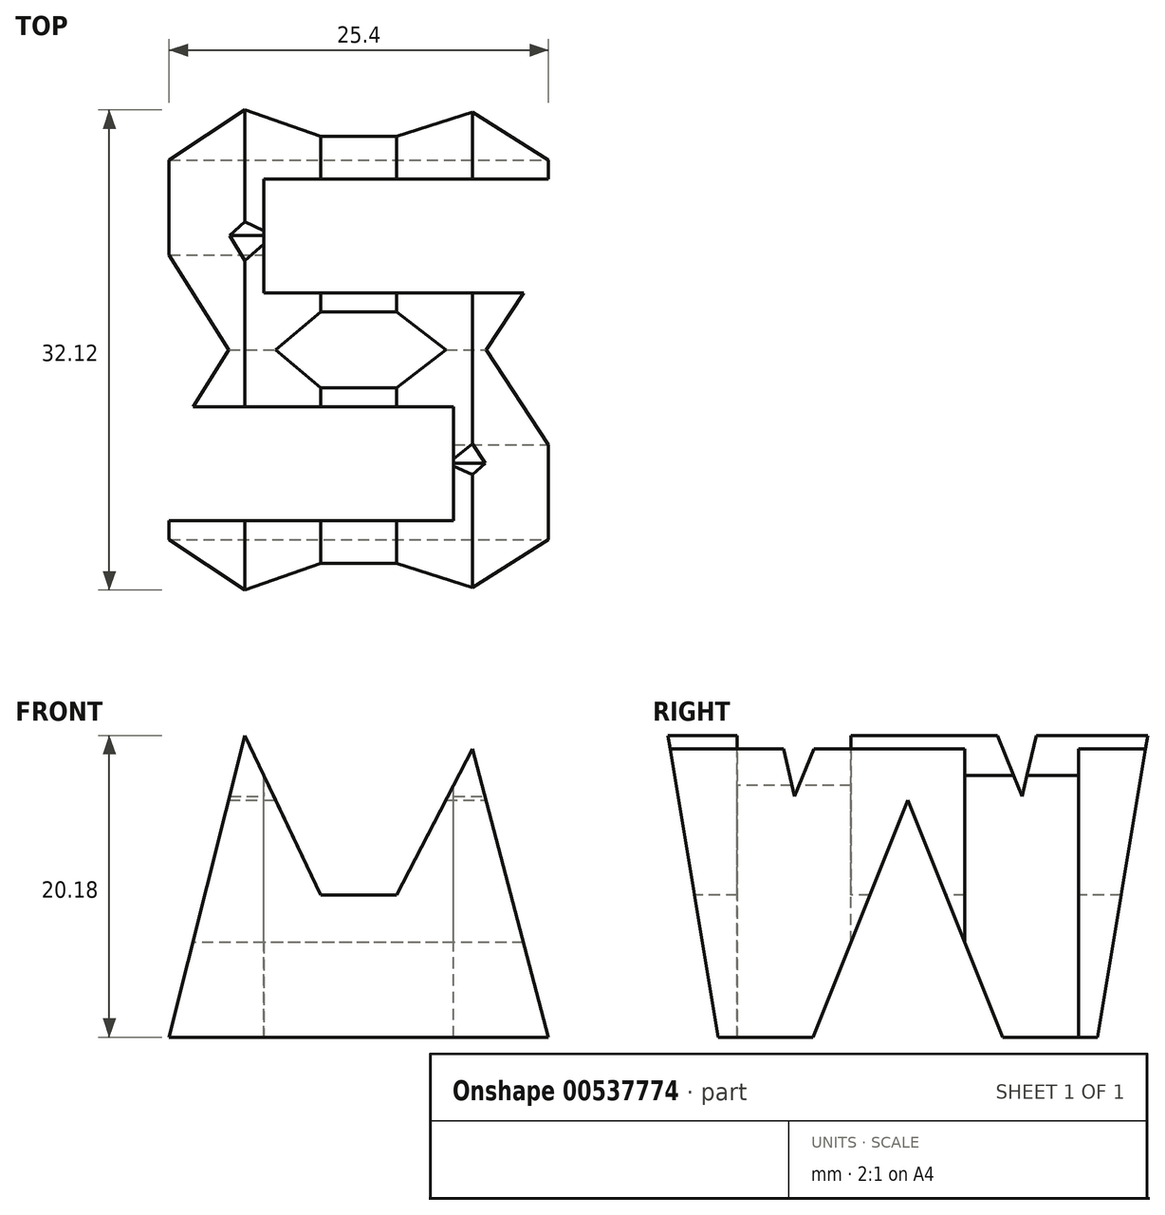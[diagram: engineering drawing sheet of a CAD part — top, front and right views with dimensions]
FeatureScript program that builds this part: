
annotation { "Feature Type Name" : "Feature", "Feature Type Description" : "" }
export const myFeature = defineFeature(function(context is Context, id is Id, definition is map)
    precondition{}
    {
        {
            var Q0;
            Q0=qCreatedBy(makeId("Front.planeOp"),FACE);
            var sketch = newSketch(context, id + "F0", { "sketchPlane" : qUnion([Q0])});
            skLineSegment(sketch, "E0", {"start": v(0, 0) * mm, "end": v(0, 38.1) * mm});
            skLineSegment(sketch, "E1", {"start": v(38.1, 38.1) * mm, "end": v(38.1, 0) * mm});
            skLineSegment(sketch, "E2", {"start": v(0, 0) * mm, "end": v(38.1, 0) * mm});
            skLineSegment(sketch, "E3", {"start": v(0, 38.1) * mm, "end": v(38.1, 38.1) * mm});
            skSolve(sketch);
        }
        {
            var Q0;
            Q0 = qSketchRegion(id + "F0", true);
            extrude(context, id + "F1", {"entities" : qUnion([Q0]), "depth" : 38.1 * mm, "offsetDistance" : 25.4 * mm});
        }
        {
            var Q0;
            Q0=qCreatedBy(makeId("Front.planeOp"),FACE);
            cPlane(context, id + "F2", {"entities" : qUnion([Q0]), "cplaneType" : CPlaneType.OFFSET, "offset" : 38.1 * mm, "width" : 152.4 * mm, "height" : 152.4 * mm});
        }
        {
            var Q0;
            Q0=qCreatedBy(makeId("Right.planeOp"),FACE);
            cPlane(context, id + "F3", {"entities" : qUnion([Q0]), "cplaneType" : CPlaneType.OFFSET, "offset" : 38.1 * mm, "width" : 152.4 * mm, "height" : 152.4 * mm});
        }
        {
            var Q0;
            Q0=qCreatedBy(makeId("Top.planeOp"),FACE);
            cPlane(context, id + "F4", {"entities" : qUnion([Q0]), "cplaneType" : CPlaneType.OFFSET, "offset" : 38.1 * mm, "width" : 152.4 * mm, "height" : 152.4 * mm});
        }
        {
            var Q0;
            Q0=qCreatedBy(id+"F3.planeOp",FACE);
            var sketch = newSketch(context, id + "F5", { "sketchPlane" : qUnion([Q0])});
            skLineSegment(sketch, "E4.bottom", {"start": v(0, 0) * mm, "end": v(-38.1, 0) * mm});
            skLineSegment(sketch, "E4.top", {"start": v(0, 38.1) * mm, "end": v(-38.1, 38.1) * mm});
            skLineSegment(sketch, "E4.left", {"start": v(0, 0) * mm, "end": v(0, 38.1) * mm});
            skLineSegment(sketch, "E4.right", {"start": v(-38.1, 0) * mm, "end": v(-38.1, 38.1) * mm});
            skLineSegment(sketch, "E5", {"start": v(-38.1, 38.1) * mm, "end": v(-31.75, 0) * mm});
            skLineSegment(sketch, "E6", {"start": v(-31.75, 38.1) * mm, "end": v(-26.64, 16.1) * mm});
            skLineSegment(sketch, "E7", {"start": v(-26.64, 16.1) * mm, "end": v(-21.56, 28.58) * mm});
            skLineSegment(sketch, "E8", {"start": v(-21.56, 28.58) * mm, "end": v(-16.48, 28.58) * mm});
            skLineSegment(sketch, "E9", {"start": v(-16.48, 28.58) * mm, "end": v(-11.4, 16.1) * mm});
            skLineSegment(sketch, "E10", {"start": v(-11.4, 16.1) * mm, "end": v(-6.35, 38.1) * mm});
            skLineSegment(sketch, "E11", {"start": v(0, 38.1) * mm, "end": v(-6.35, 0) * mm});
            skLineSegment(sketch, "E12", {"start": v(-31.75, 0) * mm, "end": v(-25.4, 0) * mm});
            skLineSegment(sketch, "E13", {"start": v(-25.4, 0) * mm, "end": v(-19.05, 15.88) * mm});
            skLineSegment(sketch, "E14", {"start": v(-19.05, 15.88) * mm, "end": v(-12.7, 0) * mm});
            skLineSegment(sketch, "E15", {"start": v(-12.7, 0) * mm, "end": v(-6.35, 0) * mm});
            skSolve(sketch);
        }
        {
            var Q0;
            {var subQ0=sQuery(id+"F5.wireOp",EDGE,"E6");Q0=makeQuery(id+"F5.imprint","IMPRINT",FACE,{"disambiguationData":[TD([[makeQuery(id+"F5.imprint","IMPRINT",EDGE,{"derivedFrom":subQ0}),1.0]])]});}
            var Q1;
            {var subQ0=sQuery(id+"F5.wireOp",EDGE,"E4.left");Q1=makeQuery(id+"F5.imprint","IMPRINT",FACE,{"disambiguationData":[TD([[makeQuery(id+"F5.imprint","IMPRINT",EDGE,{"derivedFrom":subQ0}),1.0]])]});}
            var Q2;
            {var subQ0=sQuery(id+"F5.wireOp",EDGE,"E13");Q2=makeQuery(id+"F5.imprint","IMPRINT",FACE,{"disambiguationData":[TD([[makeQuery(id+"F5.imprint","IMPRINT",EDGE,{"derivedFrom":subQ0}),-1.0]])]});}
            var Q3;
            {var subQ0=sQuery(id+"F5.wireOp",EDGE,"E4.right");Q3=makeQuery(id+"F5.imprint","IMPRINT",FACE,{"disambiguationData":[TD([[makeQuery(id+"F5.imprint","IMPRINT",EDGE,{"derivedFrom":subQ0}),-1.0]])]});}
            extrude(context, id + "F6", {"entities" : qUnion([Q0, Q1, Q2, Q3]), "operationType" : NewBodyOperationType.REMOVE, "oppositeDirection" : true, "depth" : 38.1 * mm, "offsetDistance" : 25.4 * mm});
        }
        {
            var Q0;
            Q0=qCreatedBy(id+"F2.planeOp",FACE);
            var sketch = newSketch(context, id + "F7", { "sketchPlane" : qUnion([Q0])});
            skLineSegment(sketch, "E16", {"start": v(0, 0) * mm, "end": v(0, 38.1) * mm});
            skLineSegment(sketch, "E17", {"start": v(0, 38.1) * mm, "end": v(38.1, 38.1) * mm});
            skLineSegment(sketch, "E18", {"start": v(38.1, 38.1) * mm, "end": v(38.1, 0) * mm});
            skLineSegment(sketch, "E19", {"start": v(38.1, 0) * mm, "end": v(0, 0) * mm});
            skLineSegment(sketch, "E20", {"start": v(38.1, 0) * mm, "end": v(31.75, 38.1) * mm});
            skLineSegment(sketch, "E21", {"start": v(31.75, 38.1) * mm, "end": v(25.4, 38.1) * mm});
            skLineSegment(sketch, "E22", {"start": v(25.4, 38.1) * mm, "end": v(19.05, 22.22) * mm});
            skLineSegment(sketch, "E23", {"start": v(19.05, 22.22) * mm, "end": v(12.7, 38.1) * mm});
            skLineSegment(sketch, "E24", {"start": v(12.7, 38.1) * mm, "end": v(6.35, 38.1) * mm});
            skLineSegment(sketch, "E25", {"start": v(6.35, 38.1) * mm, "end": v(0, 0) * mm});
            skLineSegment(sketch, "E26", {"start": v(38.1, 0) * mm, "end": v(31.75, 0) * mm});
            skLineSegment(sketch, "E27", {"start": v(6.35, 0) * mm, "end": v(0, 0) * mm});
            skLineSegment(sketch, "E28", {"start": v(31.75, 0) * mm, "end": v(26.67, 19.3) * mm});
            skLineSegment(sketch, "E29", {"start": v(26.67, 19.3) * mm, "end": v(21.6, 9.52) * mm});
            skLineSegment(sketch, "E30", {"start": v(21.6, 9.52) * mm, "end": v(16.51, 9.52) * mm});
            skLineSegment(sketch, "E31", {"start": v(16.51, 9.52) * mm, "end": v(11.43, 20.18) * mm});
            skLineSegment(sketch, "E32", {"start": v(11.43, 20.18) * mm, "end": v(6.35, 0) * mm});
            skSolve(sketch);
        }
        {
            var Q0;
            {var subQ0=sQuery(id+"F7.wireOp",EDGE,"E16");Q0=makeQuery(id+"F7.imprint","IMPRINT",FACE,{"disambiguationData":[TD([[makeQuery(id+"F7.imprint","IMPRINT",EDGE,{"derivedFrom":subQ0}),-1.0]])]});}
            var Q1;
            {var subQ0=sQuery(id+"F7.wireOp",EDGE,"E22");Q1=makeQuery(id+"F7.imprint","IMPRINT",FACE,{"disambiguationData":[TD([[makeQuery(id+"F7.imprint","IMPRINT",EDGE,{"derivedFrom":subQ0}),-1.0]])]});}
            var Q2;
            {var subQ0=sQuery(id+"F7.wireOp",EDGE,"E18");Q2=makeQuery(id+"F7.imprint","IMPRINT",FACE,{"disambiguationData":[TD([[makeQuery(id+"F7.imprint","IMPRINT",EDGE,{"derivedFrom":subQ0}),-1.0]])]});}
            var Q3;
            Q3=makeQuery(id+"F7.imprint","IMPRINT",FACE,{"disambiguationData":[TD([[makeQuery(id+"F7.imprint","IMPRINT",EDGE,{"derivedFrom":sQuery(id+"F7.wireOp",EDGE,"E19")}),-1.0]])]});
            extrude(context, id + "F8", {"entities" : qUnion([Q0, Q1, Q2, Q3]), "operationType" : NewBodyOperationType.REMOVE, "oppositeDirection" : true, "depth" : 38.1 * mm, "offsetDistance" : 25.4 * mm});
        }
        {
            var Q0;
            Q0=qCreatedBy(id+"F4.planeOp",FACE);
            var sketch = newSketch(context, id + "F9", { "sketchPlane" : qUnion([Q0])});
            skLineSegment(sketch, "E33", {"start": v(0, 0) * mm, "end": v(0, -38.1) * mm});
            skLineSegment(sketch, "E34", {"start": v(0, -38.1) * mm, "end": v(38.1, -38.1) * mm});
            skLineSegment(sketch, "E35", {"start": v(38.1, -38.1) * mm, "end": v(38.1, 0) * mm});
            skLineSegment(sketch, "E36", {"start": v(38.1, 0) * mm, "end": v(0, 0) * mm});
            skLineSegment(sketch, "E37", {"start": v(38.1, -7.62) * mm, "end": v(12.7, -7.62) * mm});
            skLineSegment(sketch, "E38", {"start": v(12.7, -7.62) * mm, "end": v(12.7, -15.24) * mm});
            skLineSegment(sketch, "E39", {"start": v(12.7, -15.24) * mm, "end": v(38.1, -15.24) * mm});
            skLineSegment(sketch, "E40", {"start": v(0, -22.86) * mm, "end": v(25.4, -22.86) * mm});
            skLineSegment(sketch, "E41", {"start": v(25.4, -22.86) * mm, "end": v(25.4, -30.48) * mm});
            skLineSegment(sketch, "E42", {"start": v(25.4, -30.48) * mm, "end": v(0, -30.48) * mm});
            skSolve(sketch);
        }
        {
            var Q0;
            {var subQ0=sQuery(id+"F9.wireOp",EDGE,"E40");Q0=makeQuery(id+"F9.imprint","IMPRINT",FACE,{"disambiguationData":[TD([[makeQuery(id+"F9.imprint","IMPRINT",EDGE,{"derivedFrom":subQ0}),-1.0]])]});}
            var Q1;
            {var subQ0=sQuery(id+"F9.wireOp",EDGE,"E37");Q1=makeQuery(id+"F9.imprint","IMPRINT",FACE,{"disambiguationData":[TD([[makeQuery(id+"F9.imprint","IMPRINT",EDGE,{"derivedFrom":subQ0}),1.0]])]});}
            extrude(context, id + "F10", {"entities" : qUnion([Q0, Q1]), "operationType" : NewBodyOperationType.REMOVE, "oppositeDirection" : true, "depth" : 38.1 * mm, "offsetDistance" : 25.4 * mm});
        }
    });
